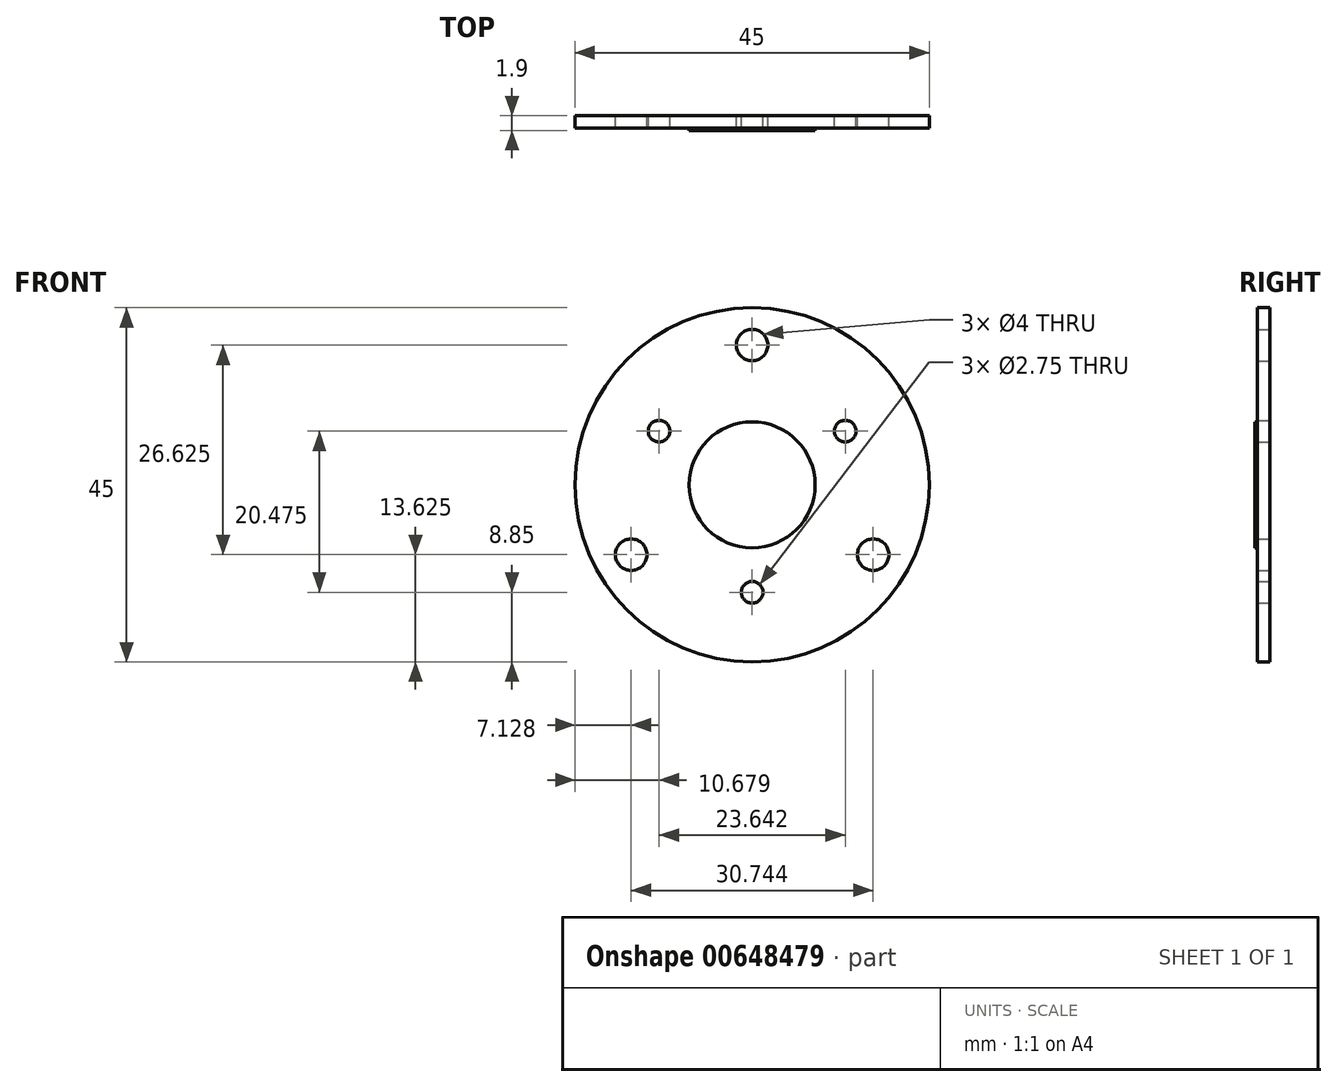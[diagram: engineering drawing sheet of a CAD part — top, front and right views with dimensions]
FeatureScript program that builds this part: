
annotation { "Feature Type Name" : "Feature", "Feature Type Description" : "" }
export const myFeature = defineFeature(function(context is Context, id is Id, definition is map)
    precondition{}
    {
        {
            var Q0;
            Q0=qCreatedBy(makeId("Front.planeOp"),FACE);
            var sketch = newSketch(context, id + "F0", { "sketchPlane" : qUnion([Q0])});
            skCircle(sketch, "E0", {"center": v(0, 0) * mm, "radius": 22.5 * mm});
            skSolve(sketch);
        }
        {
            var Q0;
            Q0=makeQuery(id+"F0.imprint","IMPRINT",FACE,{"disambiguationData":[TD([[makeQuery(id+"F0.imprint","IMPRINT",EDGE,{"derivedFrom":sQuery(id+"F0.wireOp",EDGE,"E0")}),1.0]])]});
            extrude(context, id + "F1", {"entities" : qUnion([Q0]), "depth" : 1.6 * mm, "offsetDistance" : 25 * mm});
        }
        {
            var Q0;
            Q0=makeQuery(id+"F1.opExtrude","CAP_FACE",FACE,{"disambiguationData":[OSD([sQuery(id+"F0.wireOp",EDGE,"E0")])],"isStart":false});
            var sketch = newSketch(context, id + "F2", { "sketchPlane" : qUnion([Q0])});
            skCircle(sketch, "E1", {"center": v(0, 0) * mm, "radius": 8 * mm});
            skSolve(sketch);
        }
        {
            var Q0;
            Q0=makeQuery(id+"F2.imprint","IMPRINT",FACE,{"disambiguationData":[TD([[makeQuery(id+"F2.imprint","IMPRINT",EDGE,{"derivedFrom":sQuery(id+"F2.wireOp",EDGE,"E1")}),1.0]])]});
            extrude(context, id + "F3", {"entities" : qUnion([Q0]), "operationType" : NewBodyOperationType.ADD, "depth" : 0.3 * mm, "offsetDistance" : 25 * mm});
        }
        {
            var Q0;
            Q0=makeQuery(id+"F1.opExtrude","CAP_FACE",FACE,{"disambiguationData":[OSD([sQuery(id+"F0.wireOp",EDGE,"E0")])],"isStart":true});
            var sketch = newSketch(context, id + "F4", { "sketchPlane" : qUnion([Q0])});
            skPoint(sketch, "E2", {"position": v(0, 17.75) * mm});
            skPoint(sketch, "E3.1.0", {"position": v(-15.37, -8.87) * mm});
            skPoint(sketch, "E3.2.0", {"position": v(15.37, -8.88) * mm});
            skPoint(sketch, "E3.center", {"position": v(0, 0) * mm});
            skSolve(sketch);
        }
        {
            var Q0;
            Q0=sQuery(id+"F4.wireOp",VERTEX,"E2");
            var Q1;
            Q1=sQuery(id+"F4.wireOp",VERTEX,"E3.1.0");
            var Q2;
            Q2=sQuery(id+"F4.wireOp",VERTEX,"E3.2.0");
            var Q3;
            Q3=makeQuery(id+"F1.opExtrude","SWEPT_BODY",BODY,{"disambiguationData":[OSD([sQuery(id+"F0.wireOp",EDGE,"E0")])]});
            hole(context, id + "F5", {"style" : HoleStyle.SIMPLE, "endStyle" : HoleEndStyle.THROUGH, "holeDiameter" : 4 * mm, "majorDiameter" : 5 * mm, "isTappedThrough" : true, "tappedDepth" : 12 * mm, "tapClearance" : 3, "locations" : qUnion([Q0, Q1, Q2]), "scope" : qUnion([Q3])});
        }
        {
            var Q0;
            Q0=makeQuery(id+"F1.opExtrude","CAP_FACE",FACE,{"disambiguationData":[OSD([sQuery(id+"F0.wireOp",EDGE,"E0")])],"isStart":true});
            var sketch = newSketch(context, id + "F6", { "sketchPlane" : qUnion([Q0])});
            skPoint(sketch, "E4", {"position": v(0, -13.65) * mm});
            skPoint(sketch, "E5.1.0", {"position": v(11.82, 6.82) * mm});
            skPoint(sketch, "E5.2.0", {"position": v(-11.82, 6.83) * mm});
            skPoint(sketch, "E5.center", {"position": v(0, 0) * mm});
            skSolve(sketch);
        }
        {
            var Q0;
            Q0=sQuery(id+"F6.wireOp",VERTEX,"E5.1.0");
            var Q1;
            Q1=sQuery(id+"F6.wireOp",VERTEX,"E4");
            var Q2;
            Q2=sQuery(id+"F6.wireOp",VERTEX,"E5.2.0");
            var Q3;
            Q3=makeQuery(id+"F1.opExtrude","SWEPT_BODY",BODY,{"disambiguationData":[OSD([sQuery(id+"F0.wireOp",EDGE,"E0")])]});
            hole(context, id + "F7", {"style" : HoleStyle.SIMPLE, "endStyle" : HoleEndStyle.THROUGH, "holeDiameter" : 2.75 * mm, "majorDiameter" : 5 * mm, "isTappedThrough" : true, "tappedDepth" : 12 * mm, "tapClearance" : 3, "locations" : qUnion([Q0, Q1, Q2]), "scope" : qUnion([Q3])});
        }
    });
